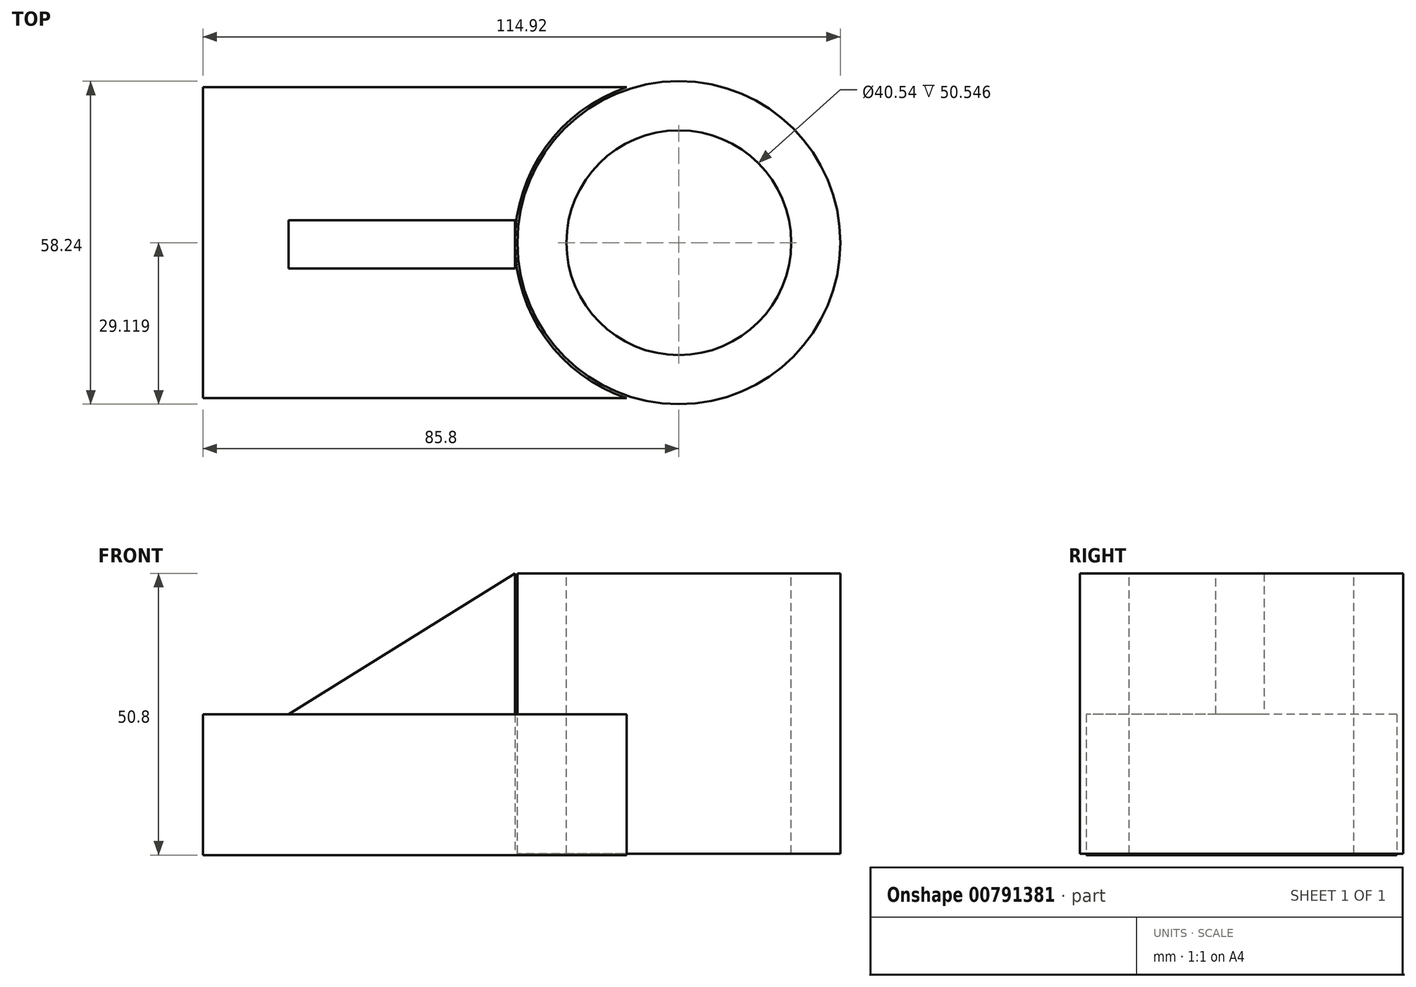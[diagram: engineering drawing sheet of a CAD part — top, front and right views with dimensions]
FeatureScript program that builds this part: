
annotation { "Feature Type Name" : "Feature", "Feature Type Description" : "" }
export const myFeature = defineFeature(function(context is Context, id is Id, definition is map)
    precondition{}
    {
        {
            var Q0;
            Q0=qCreatedBy(makeId("Top.planeOp"),FACE);
            var sketch = newSketch(context, id + "F0", { "sketchPlane" : qUnion([Q0])});
            skLineSegment(sketch, "E0.bottom", {"start": v(-76.37, 0) * mm, "end": v(0, 0) * mm});
            skLineSegment(sketch, "E0.top", {"start": v(-76.37, -56.04) * mm, "end": v(0, -56.04) * mm});
            skLineSegment(sketch, "E0.left", {"start": v(-76.37, 0) * mm, "end": v(-76.37, -56.04) * mm});
            skLineSegment(sketch, "E0.right", {"start": v(0, 0) * mm, "end": v(0, -56.04) * mm});
            skArc(sketch, "E1", {"start": v(0, 0) * mm, "mid": v(-20.14, -28.02) * mm, "end": v(0, -56.04) * mm});
            skSolve(sketch);
        }
        {
            var Q0;
            Q0=makeQuery(id+"F0.imprint","IMPRINT",FACE,{"disambiguationData":[TD([[makeQuery(id+"F0.imprint","IMPRINT",EDGE,{"derivedFrom":sQuery(id+"F0.wireOp",EDGE,"E0.bottom")}),-1.0]])]});
            extrude(context, id + "F1", {"entities" : qUnion([Q0]), "depth" : 25.4 * mm, "offsetDistance" : 25.4 * mm});
        }
        {
            var Q0;
            Q0=makeQuery(id+"F1.opExtrude","CAP_FACE",FACE,{"disambiguationData":[OSD([sQuery(id+"F0.wireOp",EDGE,"E0.bottom"),sQuery(id+"F0.wireOp",EDGE,"E0.top"),sQuery(id+"F0.wireOp",EDGE,"E0.left"),sQuery(id+"F0.wireOp",EDGE,"E1")])],"isStart":false});
            var sketch = newSketch(context, id + "F2", { "sketchPlane" : qUnion([Q0])});
            skCircle(sketch, "E2", {"center": v(9.43, -28.02) * mm, "radius": 29.12 * mm});
            skSolve(sketch);
        }
        {
            var Q0;
            Q0=makeQuery(id+"F2.imprint","IMPRINT",FACE,{"disambiguationData":[TD([[makeQuery(id+"F2.imprint","IMPRINT",EDGE,{"derivedFrom":sQuery(id+"F2.wireOp",EDGE,"E2")}),1.0]])]});
            extrude(context, id + "F3", {"entities" : qUnion([Q0]), "oppositeDirection" : true, "depth" : 25.15 * mm, "offsetDistance" : 25.4 * mm});
        }
        {
            var Q0;
            Q0=makeQuery(id+"F3.opExtrude","CAP_FACE",FACE,{"disambiguationData":[OSD([sQuery(id+"F2.wireOp",EDGE,"E2")])],"isStart":true});
            extrude(context, id + "F4", {"entities" : qUnion([Q0]), "operationType" : NewBodyOperationType.ADD, "depth" : 25.4 * mm, "offsetDistance" : 25.4 * mm});
        }
        {
            var Q0;
            Q0=makeQuery(id+"F1.opExtrude","CAP_FACE",FACE,{"disambiguationData":[OSD([sQuery(id+"F0.wireOp",EDGE,"E0.bottom"),sQuery(id+"F0.wireOp",EDGE,"E0.top"),sQuery(id+"F0.wireOp",EDGE,"E0.left"),sQuery(id+"F0.wireOp",EDGE,"E1")])],"isStart":false});
            var sketch = newSketch(context, id + "F5", { "sketchPlane" : qUnion([Q0])});
            skPoint(sketch, "E3.oppositeSnap0", {"position": v(-20.14, -28.02) * mm});
            skLineSegment(sketch, "E3.bottom", {"start": v(-60.94, -23.98) * mm, "end": v(-20.14, -23.98) * mm});
            skLineSegment(sketch, "E3.top", {"start": v(-60.94, -32.65) * mm, "end": v(-20.14, -32.65) * mm});
            skLineSegment(sketch, "E3.left", {"start": v(-60.94, -23.98) * mm, "end": v(-60.94, -32.65) * mm});
            skLineSegment(sketch, "E3.right", {"start": v(-20.14, -23.98) * mm, "end": v(-20.14, -32.65) * mm});
            skSolve(sketch);
        }
        {
            var Q0;
            {var subQ1=sQuery(id+"F5.wireOp",EDGE,"E3.bottom");Q0=makeQuery(id+"F5.imprint","IMPRINT",FACE,{"disambiguationData":[TD([[makeQuery(id+"F5.imprint","IMPRINT",EDGE,{"derivedFrom":subQ1}),-1.0]])]});}
            extrude(context, id + "F6", {"entities" : qUnion([Q0]), "operationType" : NewBodyOperationType.ADD, "depth" : 25.4 * mm, "offsetDistance" : 25.4 * mm});
        }
        {
            var Q0;
            Q0=makeQuery(id+"F6.opExtrude","SWEPT_FACE",FACE,{"disambiguationData":[OSD([sQuery(id+"F5.wireOp",EDGE,"E3.top")])]});
            var sketch = newSketch(context, id + "F7", { "sketchPlane" : qUnion([Q0])});
            skLineSegment(sketch, "E4", {"start": v(-60.94, 25.4) * mm, "end": v(-20.14, 50.8) * mm});
            skSolve(sketch);
        }
        {
            var Q0;
            Q0=makeQuery(id+"F7.imprint","IMPRINT",FACE,{"disambiguationData":[TD([[makeQuery(id+"F7.imprint","IMPRINT",EDGE,{"derivedFrom":sQuery(id+"F7.wireOp",EDGE,"E4")}),1.0]])]});
            extrude(context, id + "F8", {"entities" : qUnion([Q0]), "operationType" : NewBodyOperationType.REMOVE, "oppositeDirection" : true, "depth" : 47.5 * mm, "offsetDistance" : 25.4 * mm});
        }
        {
            var Q0;
            Q0=makeQuery(id+"F4.opExtrude","CAP_FACE",FACE,{"disambiguationData":[OSD([sQuery(id+"F2.wireOp",EDGE,"E2")])],"isStart":false});
            var sketch = newSketch(context, id + "F9", { "sketchPlane" : qUnion([Q0])});
            skCircle(sketch, "E5", {"center": v(9.43, -28.02) * mm, "radius": 20.27 * mm});
            skSolve(sketch);
        }
        {
            var Q0;
            Q0=makeQuery(id+"F9.imprint","IMPRINT",FACE,{"disambiguationData":[TD([[makeQuery(id+"F9.imprint","IMPRINT",EDGE,{"derivedFrom":sQuery(id+"F9.wireOp",EDGE,"E5")}),1.0]])]});
            extrude(context, id + "F10", {"entities" : qUnion([Q0]), "operationType" : NewBodyOperationType.REMOVE, "oppositeDirection" : true, "depth" : 50.8 * mm, "offsetDistance" : 25.4 * mm});
        }
    });
